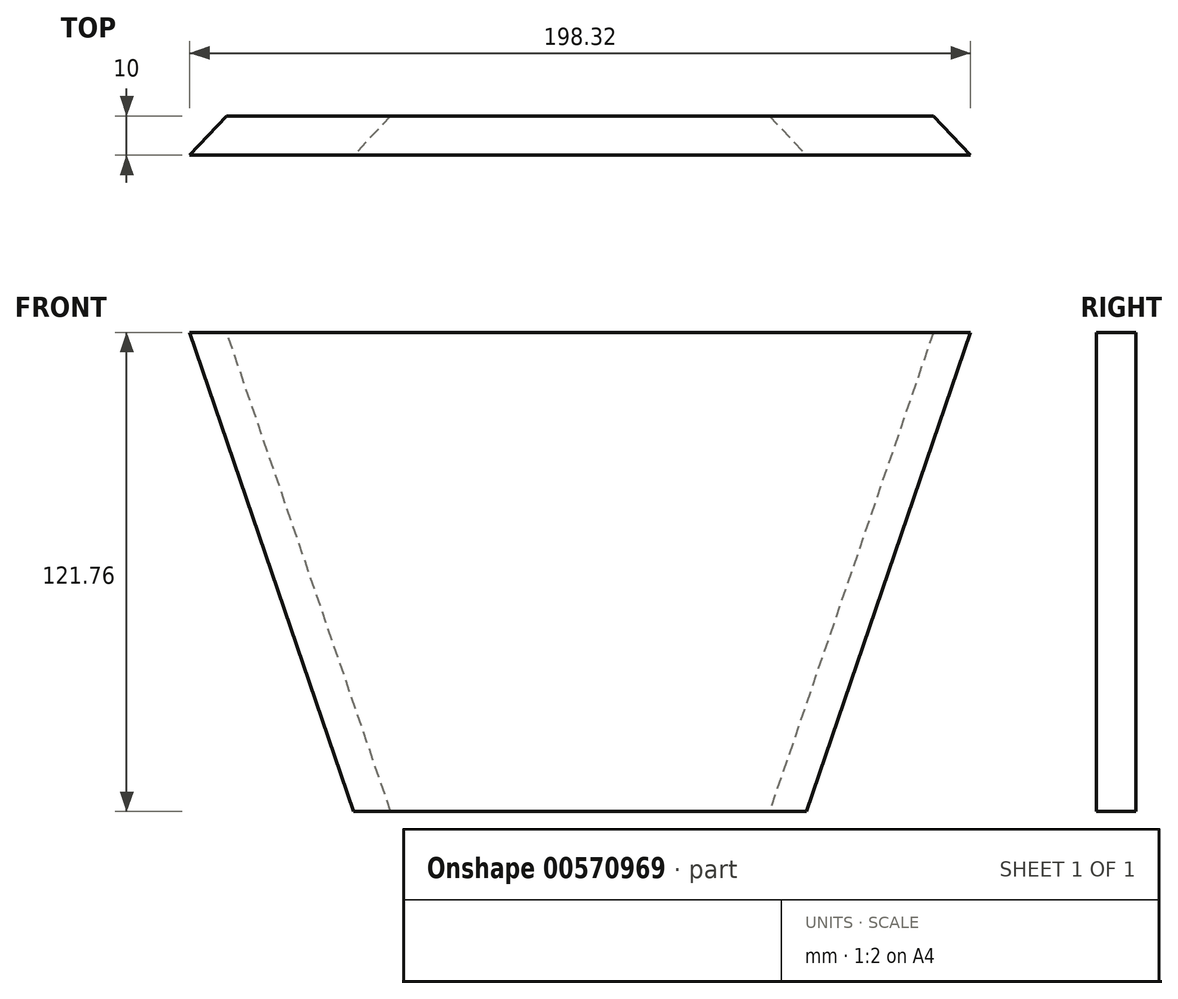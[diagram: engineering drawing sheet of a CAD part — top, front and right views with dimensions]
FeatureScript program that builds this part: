
annotation { "Feature Type Name" : "Feature", "Feature Type Description" : "" }
export const myFeature = defineFeature(function(context is Context, id is Id, definition is map)
    precondition{}
    {
        {
            var Q0;
            Q0=qCreatedBy(makeId("Front.planeOp"),FACE);
            var sketch = newSketch(context, id + "F0", { "sketchPlane" : qUnion([Q0])});
            skLineSegment(sketch, "E0.bottom", {"start": v(-93.11, 60.95) * mm, "end": v(21.89, 60.95) * mm});
            skLineSegment(sketch, "E0.top", {"start": v(-93.11, -60.81) * mm, "end": v(21.89, -60.81) * mm});
            skLineSegment(sketch, "E0.left", {"start": v(-93.11, 60.95) * mm, "end": v(-93.11, -60.81) * mm});
            skLineSegment(sketch, "E0.right", {"start": v(21.89, 60.95) * mm, "end": v(21.89, -60.81) * mm});
            skLineSegment(sketch, "E1.bottom", {"start": v(-93.11, 60.95) * mm, "end": v(-134.77, 60.95) * mm});
            skLineSegment(sketch, "E1.top", {"start": v(-93.11, 60.95) * mm, "end": v(-134.77, 60.95) * mm});
            skLineSegment(sketch, "E1.left", {"start": v(-93.11, 60.95) * mm, "end": v(-93.11, 60.95) * mm});
            skLineSegment(sketch, "E1.right", {"start": v(-134.77, 60.95) * mm, "end": v(-134.77, 60.95) * mm});
            skLineSegment(sketch, "E2.bottom", {"start": v(21.89, 60.95) * mm, "end": v(63.55, 60.95) * mm});
            skLineSegment(sketch, "E2.top", {"start": v(21.89, 60.95) * mm, "end": v(63.55, 60.95) * mm});
            skLineSegment(sketch, "E2.left", {"start": v(21.89, 60.95) * mm, "end": v(21.89, 60.95) * mm});
            skLineSegment(sketch, "E2.right", {"start": v(63.55, 60.95) * mm, "end": v(63.55, 60.95) * mm});
            skLineSegment(sketch, "E3", {"start": v(-134.77, 60.95) * mm, "end": v(-93.11, -60.81) * mm});
            skLineSegment(sketch, "E4", {"start": v(63.55, 60.95) * mm, "end": v(21.89, -60.81) * mm});
            skSolve(sketch);
        }
        {
            var Q0;
            Q0=makeQuery(id+"F0.imprint","IMPRINT",FACE,{"disambiguationData":[TD([[makeQuery(id+"F0.imprint","IMPRINT",EDGE,{"derivedFrom":sQuery(id+"F0.wireOp",EDGE,"E0.bottom")}),-1.0]])]});
            var Q1;
            Q1=makeQuery(id+"F0.imprint","IMPRINT",FACE,{"disambiguationData":[TD([[makeQuery(id+"F0.imprint","IMPRINT",EDGE,{"derivedFrom":sQuery(id+"F0.wireOp",EDGE,"E0.left")}),-1.0]])]});
            var Q2;
            Q2=makeQuery(id+"F0.imprint","IMPRINT",FACE,{"disambiguationData":[TD([[makeQuery(id+"F0.imprint","IMPRINT",EDGE,{"derivedFrom":sQuery(id+"F0.wireOp",EDGE,"E0.right")}),1.0]])]});
            extrude(context, id + "F1", {"entities" : qUnion([Q0, Q1, Q2]), "depth" : 10 * mm, "offsetDistance" : 25 * mm});
        }
        {
            var Q0;
            Q0=makeQuery(id+"F1.opExtrude","CAP_EDGE",EDGE,{"disambiguationData":[OSD([sQuery(id+"F0.wireOp",EDGE,"E3")])],"isStart":true});
            chamfer(context, id + "F2", {"entities" : qUnion([Q0]), "chamferType" : ChamferType.TWO_OFFSETS, "width1" : 10 * mm, "oppositeDirection" : false, "width2" : 8.9 * mm, "tangentPropagation" : true});
        }
        {
            var Q0;
            Q0=makeQuery(id+"F1.opExtrude","CAP_EDGE",EDGE,{"disambiguationData":[OSD([sQuery(id+"F0.wireOp",EDGE,"E4")])],"isStart":true});
            chamfer(context, id + "F3", {"entities" : qUnion([Q0]), "chamferType" : ChamferType.TWO_OFFSETS, "width1" : 8.9 * mm, "oppositeDirection" : false, "width2" : 10 * mm, "tangentPropagation" : true});
        }
    });
